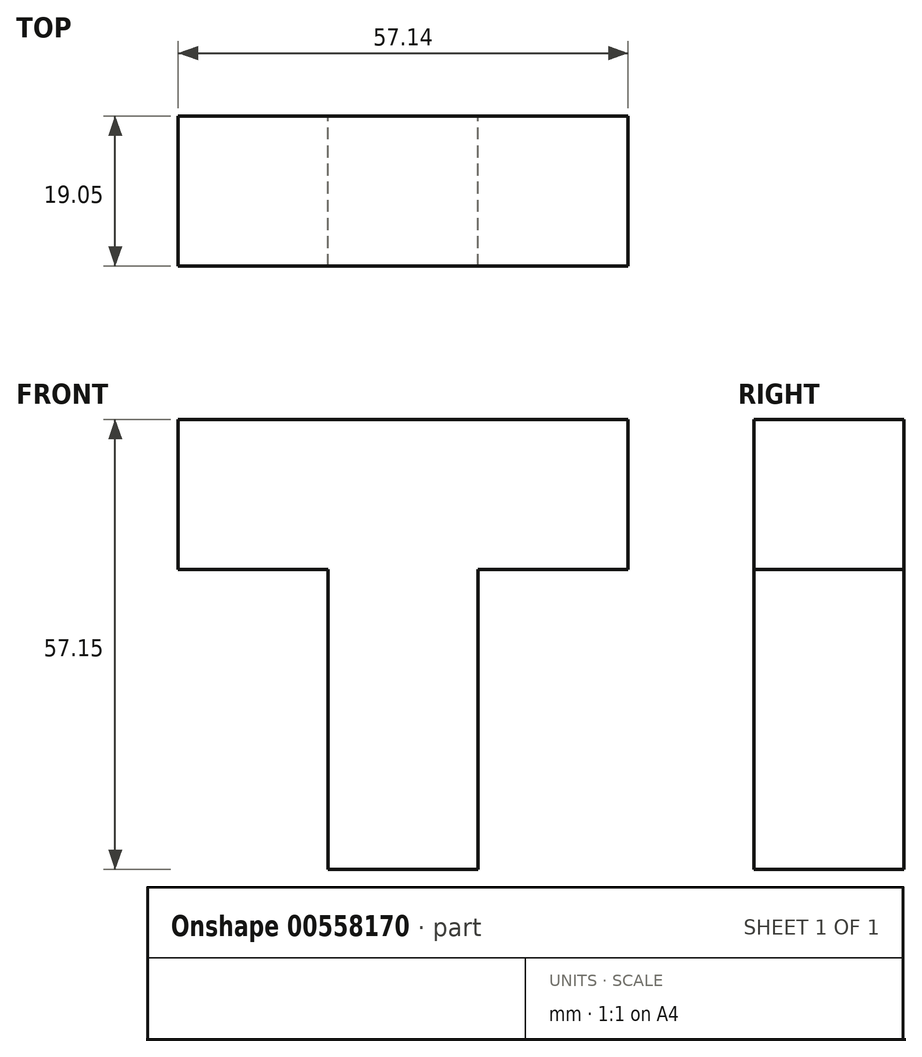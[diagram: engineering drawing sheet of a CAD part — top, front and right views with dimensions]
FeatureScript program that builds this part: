
annotation { "Feature Type Name" : "Feature", "Feature Type Description" : "" }
export const myFeature = defineFeature(function(context is Context, id is Id, definition is map)
    precondition{}
    {
        {
            var Q0;
            Q0=qCreatedBy(makeId("Front.planeOp"),FACE);
            var sketch = newSketch(context, id + "F0", { "sketchPlane" : qUnion([Q0])});
            skLineSegment(sketch, "E0", {"start": v(0, 0) * mm, "end": v(28.58, 0) * mm});
            skLineSegment(sketch, "E1", {"start": v(0, 0) * mm, "end": v(-28.58, 0) * mm});
            skLineSegment(sketch, "E2", {"start": v(-28.58, 0) * mm, "end": v(-28.58, -19.05) * mm});
            skLineSegment(sketch, "E3", {"start": v(-28.58, -19.05) * mm, "end": v(-9.53, -19.05) * mm});
            skLineSegment(sketch, "E4", {"start": v(-9.53, -19.05) * mm, "end": v(-9.53, -57.15) * mm});
            skLineSegment(sketch, "E5", {"start": v(-9.53, -57.15) * mm, "end": v(9.52, -57.15) * mm});
            skLineSegment(sketch, "E6", {"start": v(9.52, -57.15) * mm, "end": v(9.52, -19.05) * mm});
            skLineSegment(sketch, "E7", {"start": v(9.52, -19.05) * mm, "end": v(28.58, -19.05) * mm});
            skLineSegment(sketch, "E8", {"start": v(28.58, -19.05) * mm, "end": v(28.58, 0) * mm});
            skSolve(sketch);
        }
        {
            var Q0;
            Q0 = qSketchRegion(id + "F0", true);
            extrude(context, id + "F1", {"entities" : qUnion([Q0]), "depth" : 19.05 * mm, "offsetDistance" : 25.4 * mm});
        }
    });
